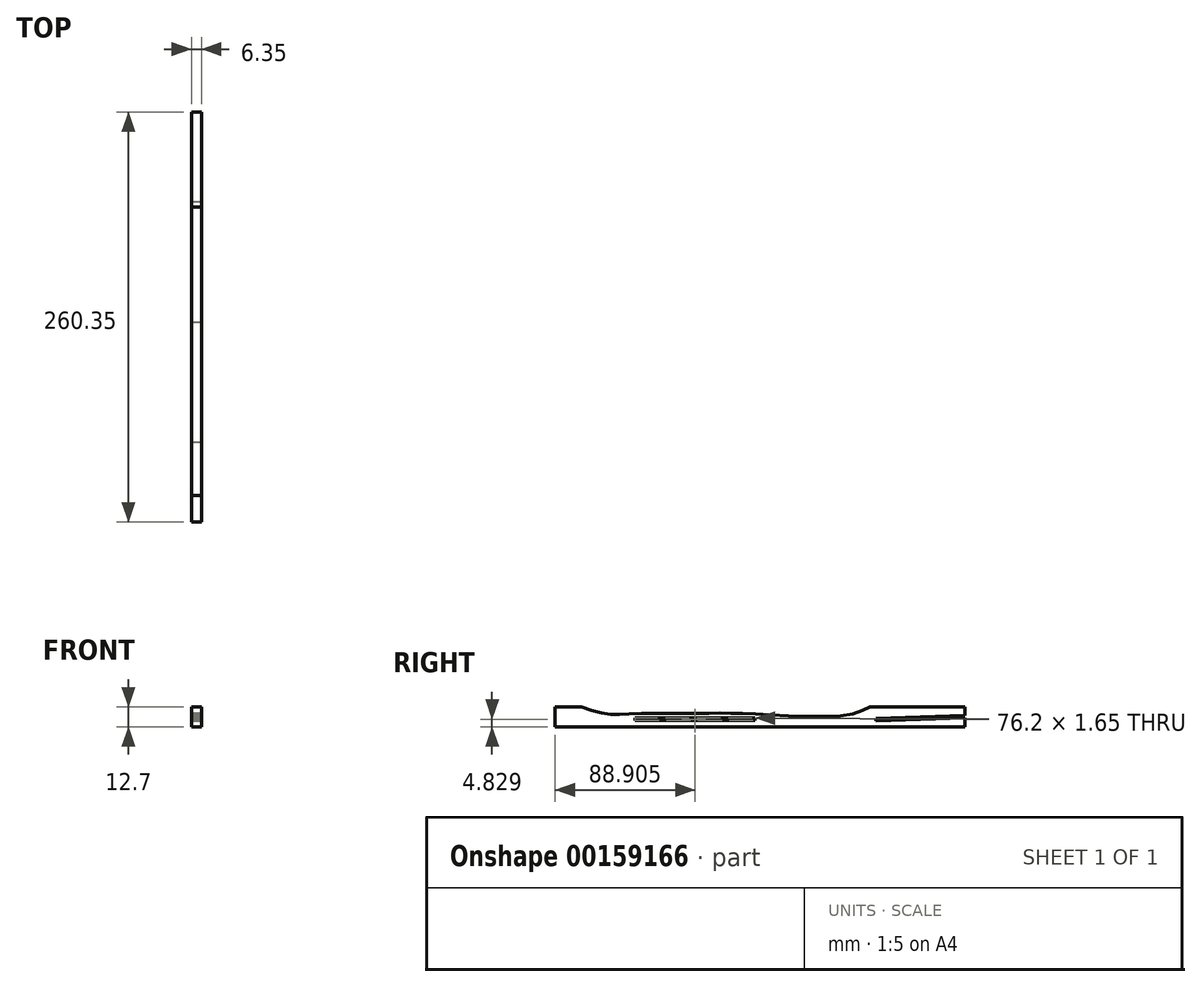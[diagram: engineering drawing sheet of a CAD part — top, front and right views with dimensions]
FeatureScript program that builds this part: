
annotation { "Feature Type Name" : "Feature", "Feature Type Description" : "" }
export const myFeature = defineFeature(function(context is Context, id is Id, definition is map)
    precondition{}
    {
        {
            var Q0;
            Q0=qCreatedBy(makeId("Right.planeOp"),FACE);
            var sketch = newSketch(context, id + "F0", { "sketchPlane" : qUnion([Q0])});
            skLineSegment(sketch, "E0.bottom", {"start": v(99.07, 15.52) * mm, "end": v(-161.28, 15.52) * mm});
            skLineSegment(sketch, "E0.top", {"start": v(99.07, 28.22) * mm, "end": v(-161.28, 28.22) * mm});
            skLineSegment(sketch, "E0.left", {"start": v(99.07, 15.52) * mm, "end": v(99.07, 28.22) * mm});
            skLineSegment(sketch, "E0.right", {"start": v(-161.28, 15.52) * mm, "end": v(-161.28, 28.22) * mm});
            skPoint(sketch, "E0.middle", {"position": v(-31.1, 21.87) * mm});
            skSolve(sketch);
        }
        {
            var Q0;
            Q0 = qSketchRegion(id + "F0", true);
            extrude(context, id + "F1", {"entities" : qUnion([Q0]), "depth" : 6.35 * mm});
        }
        {
            var Q0;
            Q0=makeQuery(id+"F1.opExtrude","CAP_FACE",FACE,{"disambiguationData":[OSD([sQuery(id+"F0.wireOp",EDGE,"E0.bottom"),sQuery(id+"F0.wireOp",EDGE,"E0.top"),sQuery(id+"F0.wireOp",EDGE,"E0.left"),sQuery(id+"F0.wireOp",EDGE,"E0.right")])],"isStart":false});
            var sketch = newSketch(context, id + "F2", { "sketchPlane" : qUnion([Q0])});
            skLineSegment(sketch, "E1", {"start": v(99.07, 22.84) * mm, "end": v(42.28, 21.02) * mm});
            skLineSegment(sketch, "E2", {"start": v(42.28, 21.02) * mm, "end": v(42.33, 19.37) * mm});
            skLineSegment(sketch, "E3", {"start": v(42.33, 19.37) * mm, "end": v(99.07, 21.19) * mm});
            skLineSegment(sketch, "E4", {"start": v(99.07, 21.19) * mm, "end": v(99.07, 22.84) * mm});
            skSolve(sketch);
        }
        {
            var Q0;
            Q0 = qSketchRegion(id + "F2", true);
            extrude(context, id + "F3", {"entities" : qUnion([Q0]), "operationType" : NewBodyOperationType.REMOVE, "oppositeDirection" : true, "depth" : 25.4 * mm});
        }
        {
            var Q0;
            Q0=makeQuery(id+"F1.opExtrude","CAP_FACE",FACE,{"disambiguationData":[OSD([sQuery(id+"F0.wireOp",EDGE,"E0.bottom"),sQuery(id+"F0.wireOp",EDGE,"E0.top"),sQuery(id+"F0.wireOp",EDGE,"E0.left"),sQuery(id+"F0.wireOp",EDGE,"E0.right")])],"isStart":false});
            var sketch = newSketch(context, id + "F4", { "sketchPlane" : qUnion([Q0])});
            skLineSegment(sketch, "E5", {"start": v(-110.48, 28.22) * mm, "end": v(-110.48, 15.52) * mm});
            skLineSegment(sketch, "E6", {"start": v(-34.28, 28.22) * mm, "end": v(-34.28, 15.52) * mm});
            skLineSegment(sketch, "E7", {"start": v(-110.48, 21.17) * mm, "end": v(-34.28, 21.17) * mm});
            skLineSegment(sketch, "E8", {"start": v(-34.28, 21.17) * mm, "end": v(-34.28, 19.52) * mm});
            skLineSegment(sketch, "E9", {"start": v(-34.28, 19.52) * mm, "end": v(-110.48, 19.52) * mm});
            skLineSegment(sketch, "E10", {"start": v(-110.48, 19.52) * mm, "end": v(-110.48, 21.17) * mm});
            skSolve(sketch);
        }
        {
            var Q0;
            Q0 = qSketchRegion(id + "F4", true);
            extrude(context, id + "F5", {"entities" : qUnion([Q0]), "operationType" : NewBodyOperationType.REMOVE, "oppositeDirection" : true, "depth" : 25.4 * mm});
        }
        {
            var Q0;
            Q0=makeQuery(id+"F1.opExtrude","CAP_FACE",FACE,{"disambiguationData":[OSD([sQuery(id+"F0.wireOp",EDGE,"E0.bottom"),sQuery(id+"F0.wireOp",EDGE,"E0.top"),sQuery(id+"F0.wireOp",EDGE,"E0.left"),sQuery(id+"F0.wireOp",EDGE,"E0.right")])],"isStart":false});
            var sketch = newSketch(context, id + "F6", { "sketchPlane" : qUnion([Q0])});
            skFitSpline(sketch, "E11", {"points": [v(38.74, 28.22) * mm, v(22.67, 22.93) * mm, v(-27.78, 23.4) * mm, v(-54.77, 24.27) * mm, v(-78, 23.95) * mm, v(-112.06, 23.9) * mm, v(-127.42, 23.62) * mm, v(-144.57, 28.22) * mm], "startDerivative": vector(-110.96, -54.59) * mm, "endDerivative": vector(-149.39, 49.8) * mm});
            skLineSegment(sketch, "E12", {"start": v(-144.57, 28.22) * mm, "end": v(38.74, 28.22) * mm});
            skSolve(sketch);
        }
        {
            var Q0;
            Q0 = qSketchRegion(id + "F6", true);
            extrude(context, id + "F7", {"entities" : qUnion([Q0]), "operationType" : NewBodyOperationType.REMOVE, "oppositeDirection" : true, "depth" : 25.4 * mm});
        }
    });
